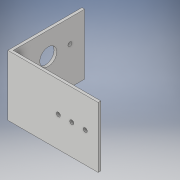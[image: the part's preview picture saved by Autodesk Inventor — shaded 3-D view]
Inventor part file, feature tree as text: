
AUTODESK INVENTOR PART (.ipt)
format: ipt  version: 2019 (Build 230136000, 136)  size: 142,848 bytes
history: native  units: mm
features: sketch x5, extrude x3, hole x2, other x1
ambient origin geometry x8: Origin, YZ Plane, XZ Plane, XY Plane, X Axis, Y Axis, Z Axis, Center Point
bodies: Body1 (feature_tree)
feature tree (11):
  other  "ソリッド1"
  extrude  "押し出し1"  Depth=65.0mm
  extrude  "押し出し2"  Depth=45.0mm
  extrude  "押し出し3"  Depth=2.0mm TaperAngle=0.0deg
  hole  "穴1"  [1 undecoded]
  hole  "穴2"  [1 undecoded]
  sketch  "スケッチ1"
  sketch  "スケッチ2"
  sketch  "スケッチ3"
  sketch  "スケッチ4"
  sketch  "スケッチ5"
note: 2 required parameter values undecoded (feature->parameter linkage not recoverable at this tier; creation-order binding heuristic only, values carry confidence <= 0.55)
